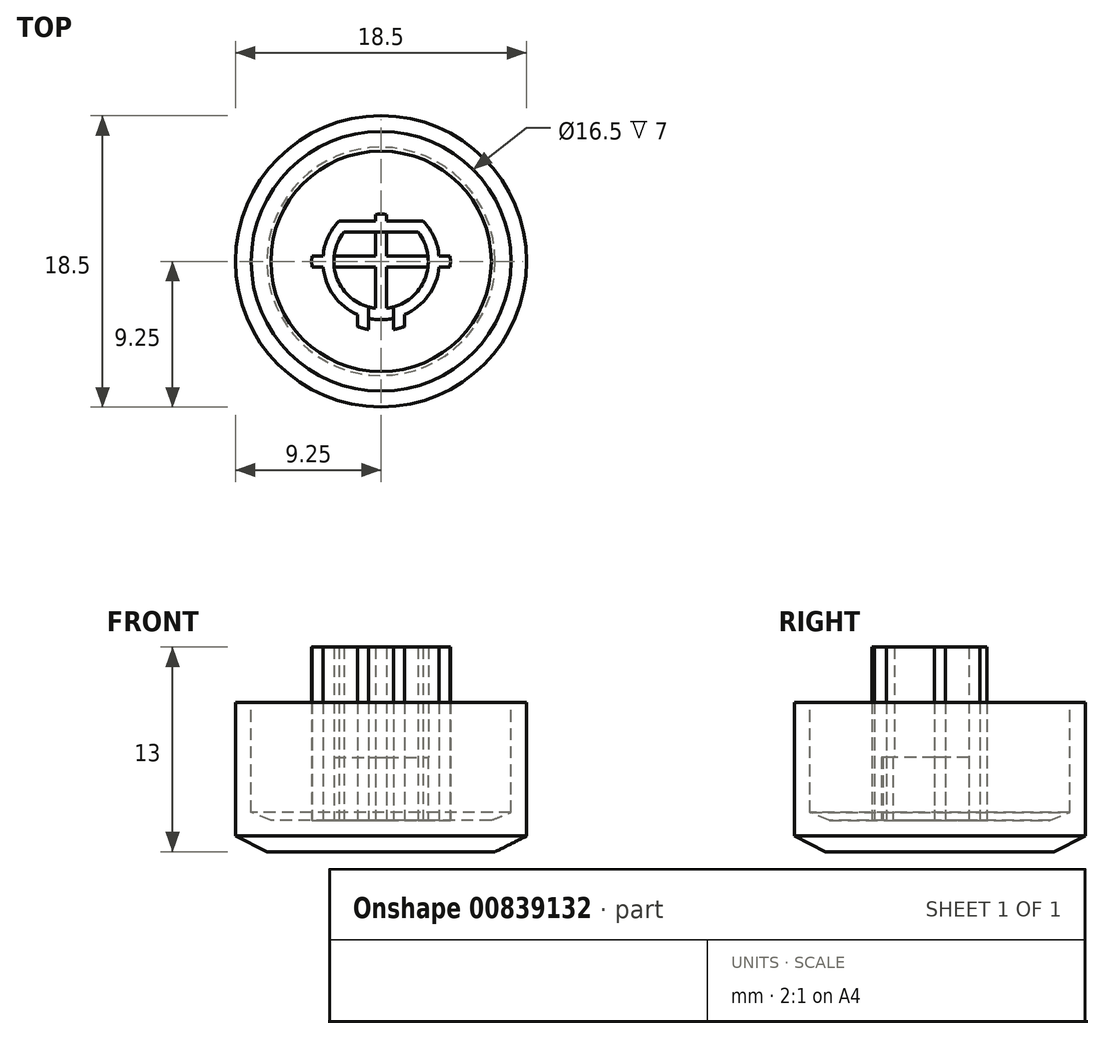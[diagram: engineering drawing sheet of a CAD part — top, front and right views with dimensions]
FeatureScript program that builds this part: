
annotation { "Feature Type Name" : "Feature", "Feature Type Description" : "" }
export const myFeature = defineFeature(function(context is Context, id is Id, definition is map)
    precondition{}
    {
        {
            var Q0;
            Q0=qCreatedBy(makeId("Front.planeOp"),FACE);
            var sketch = newSketch(context, id + "F0", { "sketchPlane" : qUnion([Q0])});
            skLineSegment(sketch, "E0", {"start": v(0, 7.05) * mm, "end": v(0, -7.62) * mm, "construction": true});
            skLineSegment(sketch, "E1", {"start": v(0, 0) * mm, "end": v(7.25, 0) * mm});
            skLineSegment(sketch, "E2", {"start": v(7.25, 0) * mm, "end": v(9.25, 1) * mm});
            skLineSegment(sketch, "E3", {"start": v(9.25, 1) * mm, "end": v(9.25, 9.5) * mm});
            skLineSegment(sketch, "E4", {"start": v(8.25, 9.5) * mm, "end": v(8.25, 2.5) * mm});
            skLineSegment(sketch, "E5", {"start": v(7, 2) * mm, "end": v(0, 2) * mm});
            skLineSegment(sketch, "E6", {"start": v(8.25, 9.5) * mm, "end": v(9.25, 9.5) * mm});
            skLineSegment(sketch, "E7", {"start": v(0, 2) * mm, "end": v(0, 0) * mm});
            skLineSegment(sketch, "E8.trimOffspring", {"start": v(8.25, 2.5) * mm, "end": v(7, 2) * mm});
            skSolve(sketch);
        }
        {
            var Q0;
            Q0 = qSketchRegion(id + "F0", true);
            var Q1;
            Q1=sQuery(id+"F0.wireOp",EDGE,"E0");
            revolve(context, id + "F1", {"surfaceOperationType" : NewSurfaceOperationType.NEW, "entities" : qUnion([Q0]), "axis" : qUnion([Q1]), "revolveType" : RevolveType.FULL});
        }
        {
            var Q0;
            Q0=qCreatedBy(makeId("Top.planeOp"),FACE);
            var sketch = newSketch(context, id + "F2", { "sketchPlane" : qUnion([Q0])});
            skArc(sketch, "E9", {"start": v(0.35, 2.98) * mm, "mid": v(0, 3) * mm, "end": v(-0.35, 2.98) * mm});
            skArc(sketch, "E10", {"start": v(-2.68, 2.55) * mm, "mid": v(-3.63, -0.73) * mm, "end": v(-1.49, -3.39) * mm});
            skLineSegment(sketch, "E11", {"start": v(-2.68, 2.55) * mm, "end": v(2.68, 2.55) * mm});
            skLineSegment(sketch, "E12", {"start": v(-2.36, 1.85) * mm, "end": v(2.36, 1.85) * mm});
            skLineSegment(sketch, "E13", {"start": v(-4.39, 0.35) * mm, "end": v(-0.35, 0.35) * mm});
            skLineSegment(sketch, "E14", {"start": v(-4.39, -0.35) * mm, "end": v(-0.35, -0.35) * mm});
            skLineSegment(sketch, "E15", {"start": v(-0.35, 2.98) * mm, "end": v(-0.35, 0.35) * mm});
            skLineSegment(sketch, "E16", {"start": v(0.35, 2.98) * mm, "end": v(0.35, 0.35) * mm});
            skLineSegment(sketch, "E17", {"start": v(-0.79, -2.9) * mm, "end": v(-0.79, -4.33) * mm});
            skLineSegment(sketch, "E18", {"start": v(0.79, -2.9) * mm, "end": v(0.79, -4.33) * mm});
            skLineSegment(sketch, "E19", {"start": v(0, 3.7) * mm, "end": v(0, -3.7) * mm, "construction": true});
            skLineSegment(sketch, "E20", {"start": v(3.7, 0) * mm, "end": v(-3.7, 0) * mm, "construction": true});
            skArc(sketch, "E21", {"start": v(-4.39, 0.35) * mm, "mid": v(-4.4, 0) * mm, "end": v(-4.39, -0.35) * mm});
            skLineSegment(sketch, "E22", {"start": v(-1.49, -3.39) * mm, "end": v(-1.49, -4.14) * mm});
            skLineSegment(sketch, "E23", {"start": v(1.49, -3.39) * mm, "end": v(1.49, -4.14) * mm});
            skArc(sketch, "E24.trimOffspring", {"start": v(-1.49, -4.14) * mm, "mid": v(-1.14, -4.25) * mm, "end": v(-0.79, -4.33) * mm});
            skArc(sketch, "E25.trimOffspring", {"start": v(0.79, -4.33) * mm, "mid": v(1.14, -4.25) * mm, "end": v(1.49, -4.14) * mm});
            skArc(sketch, "E26.trimOffspring", {"start": v(4.39, -0.35) * mm, "mid": v(4.4, 0) * mm, "end": v(4.39, 0.35) * mm});
            skArc(sketch, "E27.trimOffspring", {"start": v(-2.36, 1.85) * mm, "mid": v(-2.77, -1.15) * mm, "end": v(-0.35, -2.98) * mm});
            skArc(sketch, "E28.trimOffspring", {"start": v(-0.79, -3.62) * mm, "mid": v(0, -3.7) * mm, "end": v(0.79, -3.62) * mm});
            skArc(sketch, "E29.trimOffspring", {"start": v(1.49, -3.39) * mm, "mid": v(3.63, -0.73) * mm, "end": v(2.68, 2.55) * mm});
            skArc(sketch, "E30.trimOffspring", {"start": v(0.35, -2.98) * mm, "mid": v(2.77, -1.15) * mm, "end": v(2.36, 1.85) * mm});
            skLineSegment(sketch, "E31.trimOffspring", {"start": v(0.35, -0.35) * mm, "end": v(0.35, -2.98) * mm});
            skLineSegment(sketch, "E32.trimOffspring", {"start": v(-0.35, -0.35) * mm, "end": v(-0.35, -2.98) * mm});
            skLineSegment(sketch, "E33.trimOffspring", {"start": v(0.35, 0.35) * mm, "end": v(4.39, 0.35) * mm});
            skLineSegment(sketch, "E34.trimOffspring", {"start": v(0.35, -0.35) * mm, "end": v(4.39, -0.35) * mm});
            skSolve(sketch);
        }
        {
            var Q0;
            {var subQ8=sQuery(id+"F2.wireOp",EDGE,"E22");Q0=makeQuery(id+"F2.imprint","IMPRINT",FACE,{"disambiguationData":[TD([[makeQuery(id+"F2.imprint","IMPRINT",EDGE,{"derivedFrom":subQ8}),1.0]])]});}
            var Q1;
            {var subQ5=sQuery(id+"F2.wireOp",EDGE,"E11");var subQ6=sQuery(id+"F2.wireOp",EDGE,"E10");var subQ7=makeQuery(id+"F2.imprint","INTERSECT",VERTEX,{"derivedFrom":[subQ6,subQ5]});Q1=makeQuery(id+"F2.imprint","IMPRINT",FACE,{"disambiguationData":[TD([[makeQuery(id+"F2.imprint","IMPRINT",EDGE,{"disambiguationData":[TD([[subQ7,-1.0]])],"derivedFrom":subQ6}),1.0]])]});}
            var Q2;
            {var subQ1=sQuery(id+"F2.wireOp",EDGE,"E11");var subQ7=sQuery(id+"F2.wireOp",EDGE,"E29.trimOffspring");var subQ8=makeQuery(id+"F2.imprint","INTERSECT",VERTEX,{"derivedFrom":[subQ1,subQ7]});Q2=makeQuery(id+"F2.imprint","IMPRINT",FACE,{"disambiguationData":[TD([[makeQuery(id+"F2.imprint","IMPRINT",EDGE,{"disambiguationData":[TD([[subQ8,1.0]])],"derivedFrom":subQ1}),-1.0]])]});}
            var Q3;
            {var subQ0=sQuery(id+"F2.wireOp",EDGE,"E34.trimOffspring");var subQ1=sQuery(id+"F2.wireOp",EDGE,"E29.trimOffspring");var subQ2=makeQuery(id+"F2.imprint","INTERSECT",VERTEX,{"derivedFrom":[subQ1,subQ0]});Q3=makeQuery(id+"F2.imprint","IMPRINT",FACE,{"disambiguationData":[TD([[makeQuery(id+"F2.imprint","IMPRINT",EDGE,{"disambiguationData":[TD([[subQ2,-1.0]])],"derivedFrom":subQ1}),1.0]])]});}
            var Q4;
            {var subQ0=sQuery(id+"F2.wireOp",EDGE,"E15");var subQ1=sQuery(id+"F2.wireOp",EDGE,"E11");var subQ2=makeQuery(id+"F2.imprint","INTERSECT",VERTEX,{"derivedFrom":[subQ1,subQ0]});Q4=makeQuery(id+"F2.imprint","IMPRINT",FACE,{"disambiguationData":[TD([[makeQuery(id+"F2.imprint","IMPRINT",EDGE,{"disambiguationData":[TD([[subQ2,-1.0]])],"derivedFrom":subQ1}),-1.0]])]});}
            var Q5;
            {var subQ0=sQuery(id+"F2.wireOp",EDGE,"E13");var subQ1=sQuery(id+"F2.wireOp",EDGE,"E10");var subQ2=makeQuery(id+"F2.imprint","INTERSECT",VERTEX,{"derivedFrom":[subQ1,subQ0]});Q5=makeQuery(id+"F2.imprint","IMPRINT",FACE,{"disambiguationData":[TD([[makeQuery(id+"F2.imprint","IMPRINT",EDGE,{"disambiguationData":[TD([[subQ2,-1.0]])],"derivedFrom":subQ1}),1.0]])]});}
            var Q6;
            {var subQ0=sQuery(id+"F2.wireOp",EDGE,"E23");Q6=makeQuery(id+"F2.imprint","IMPRINT",FACE,{"disambiguationData":[TD([[makeQuery(id+"F2.imprint","IMPRINT",EDGE,{"derivedFrom":subQ0}),-1.0]])]});}
            var Q7;
            {var subQ5=sQuery(id+"F2.wireOp",EDGE,"E21");Q7=makeQuery(id+"F2.imprint","IMPRINT",FACE,{"disambiguationData":[TD([[makeQuery(id+"F2.imprint","IMPRINT",EDGE,{"derivedFrom":subQ5}),1.0]])]});}
            var Q8;
            {var subQ0=sQuery(id+"F2.wireOp",EDGE,"E9");Q8=makeQuery(id+"F2.imprint","IMPRINT",FACE,{"disambiguationData":[TD([[makeQuery(id+"F2.imprint","IMPRINT",EDGE,{"derivedFrom":subQ0}),1.0]])]});}
            var Q9;
            {var subQ0=sQuery(id+"F2.wireOp",EDGE,"E26.trimOffspring");Q9=makeQuery(id+"F2.imprint","IMPRINT",FACE,{"disambiguationData":[TD([[makeQuery(id+"F2.imprint","IMPRINT",EDGE,{"derivedFrom":subQ0}),1.0]])]});}
            extrude(context, id + "F3", {"entities" : qUnion([Q0, Q1, Q2, Q3, Q4, Q5, Q6, Q7, Q8, Q9]), "operationType" : NewBodyOperationType.ADD, "depth" : 13 * mm, "offsetDistance" : 25 * mm});
        }
        {
            var Q0;
            {var subQ0=sQuery(id+"F2.wireOp",EDGE,"E28.trimOffspring");Q0=makeQuery(id+"F2.imprint","IMPRINT",FACE,{"disambiguationData":[TD([[makeQuery(id+"F2.imprint","IMPRINT",EDGE,{"derivedFrom":subQ0}),1.0]])]});}
            extrude(context, id + "F4", {"entities" : qUnion([Q0]), "operationType" : NewBodyOperationType.ADD, "depth" : 6 * mm, "offsetDistance" : 25 * mm});
        }
    });
